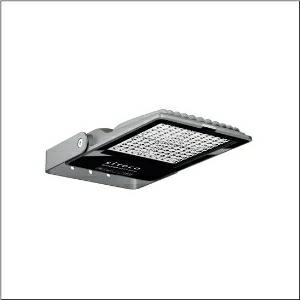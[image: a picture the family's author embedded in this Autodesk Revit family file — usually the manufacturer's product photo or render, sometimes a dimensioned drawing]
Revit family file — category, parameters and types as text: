
# Revit family: sicompact_r__31_mini___pl32_5xa7571f1k23_4385
name_source: partatom
category: Lighting Fixtures
units: mm (PartAtom-declared; Revit-internal decimal feet)

## family parameters
Cut with Voids When Loaded = No
Host = Face
Light Source = No
Part Type = Normal
Room Calculation Point = No
Round Connector Dimension = Use Diameter
Shared = No

## types (1)
- SiCompact® 31 mini  PL32 (1 x LED, 20000 lm, 130 W, 3000K)
    Apparent Load = 130 VA
    CIE Flux Codes = 32 69 98 100 100
    Color Rendering = 70
    Color Temperature = 3000K
    Default Elevation = 1800 mm
    Description = SiCompact® 31 mini, floodlight, primary light control with lens, of plastic, of toughened safety glass, transparent, light distribution: PL32, light emission: direct distribution, primary light characteristic: asymmetric, installation type: surface-mounted, LED, High Power LED, rated luminous flux: 20.000lm, luminous efficacy: 154lm/W, light colour: 730, colour temperature: 3000K, control gear: ON/OFF, with cable, 3x 1.5mm², mains connection: 220..240V, AC, 50/60Hz, connection cable pre-assembled, cable length: 2m, rated input power: 130W, of diecast aluminium, specular, metallic grey (RAL 9006), length: 461mm, width: 261mm, height: 62mm, bracket, of sheet steel, coated, metallic grey (RAL 9006), ON/OFF, protection rating (complete): IP66, insulation class (complete): insulation class I (protective earthing), certification: CE, ENEC, impact resistance: IK08, permissible operating ambient temperature: -40..+45°C, packaging unit: 1 piece

Light Distribution: PL32
    Height = 62 mm  [stored 0.203412 ft]
    Lamp = 1 x LED
    Lamp Light Flux = 20000 lm
    Lamp Power = 130 W
    Lamp count = 1
    Length = 460 mm
    Luminous efficacy = 154 lm/W
    Manufacturer = Siteco
    ModVariant = No
    Model = 5XA7571F1K23
    Mounting Place = Wall
    Mounting Type = Surface mounted
    Number of Poles = 1
    OnlyDefault = Yes
    Power Factor = 1
    Product Name = SiCompact® 31 mini | PL32
    Product group = floodlight | wall mounted
    ProductGroupID = 2001
    Protection Class = Protection class I
    Protection Degree = IP 66
    RLX_Detail_Level = 1
    RLX_Emergency_Light_Flux = 0 lm
    RLX_Emergency_Type = 0
    RLX_Emergency_Type_DB = No
    RlxData = <blob elided: 126877 chars, md5=63236b1e>
    Socket = socket
    Standby Power = 0 W
    System Light Flux = 20000 lm
    System Power = 130 W
    Type Comments = Product without accessories
    Type Image = l_1006951.jpg
    URL = http://relux.com
    VarID = ---
    Voltage = 0 V
    Weight = 0.00 kg
    Width = 260 mm

note: [stored X ft] marks values corroborated as IEEE doubles in the binary element streams (Revit-internal decimal feet)

## geometry (parser evidence)
native form markers: Blend x4, Sweep x15
no freeform markers — native parametric forms only
